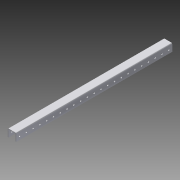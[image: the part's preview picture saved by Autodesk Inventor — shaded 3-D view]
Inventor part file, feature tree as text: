
AUTODESK INVENTOR PART (.ipt)
format: ipt  version: 2015 (Build 190159000, 159)  size: 204,288 bytes
history: native  units: in
note: dims shown in document units (in); Inventor stores cm internally (conversion verified against a paired STEP export)
features: extrude x2, sketch x2, pattern_linear x1
ambient origin geometry x8: Origin, YZ Plane, XZ Plane, XY Plane, X Axis, Y Axis, Z Axis, Center Point
bodies: Solid1 (feature_tree)
feature tree (5):
  extrude  "Extrusion1"  Depth=23.0in
  extrude  "Extrusion4"  Depth=0.5in
  pattern_linear  "Rectangular Pattern3"  Spacing1=0.0in  [1 undecoded]
  sketch  "Sketch1"  dims[d0=1.13in d1=1.25in d2=0.125in d3=0.125in d4=0.125in d5=23.0in]
  sketch  "Sketch4"  dims[d6=0.0in d34=0.5in d35=0.0in d36=0.25in d37=1.0in d38=0.0in d39=5.9055in d41=1.0in d42=5.9055in d44=1.0in]
note: 1 required parameter value undecoded (feature->parameter linkage not recoverable at this tier; creation-order binding heuristic only, values carry confidence <= 0.55)
